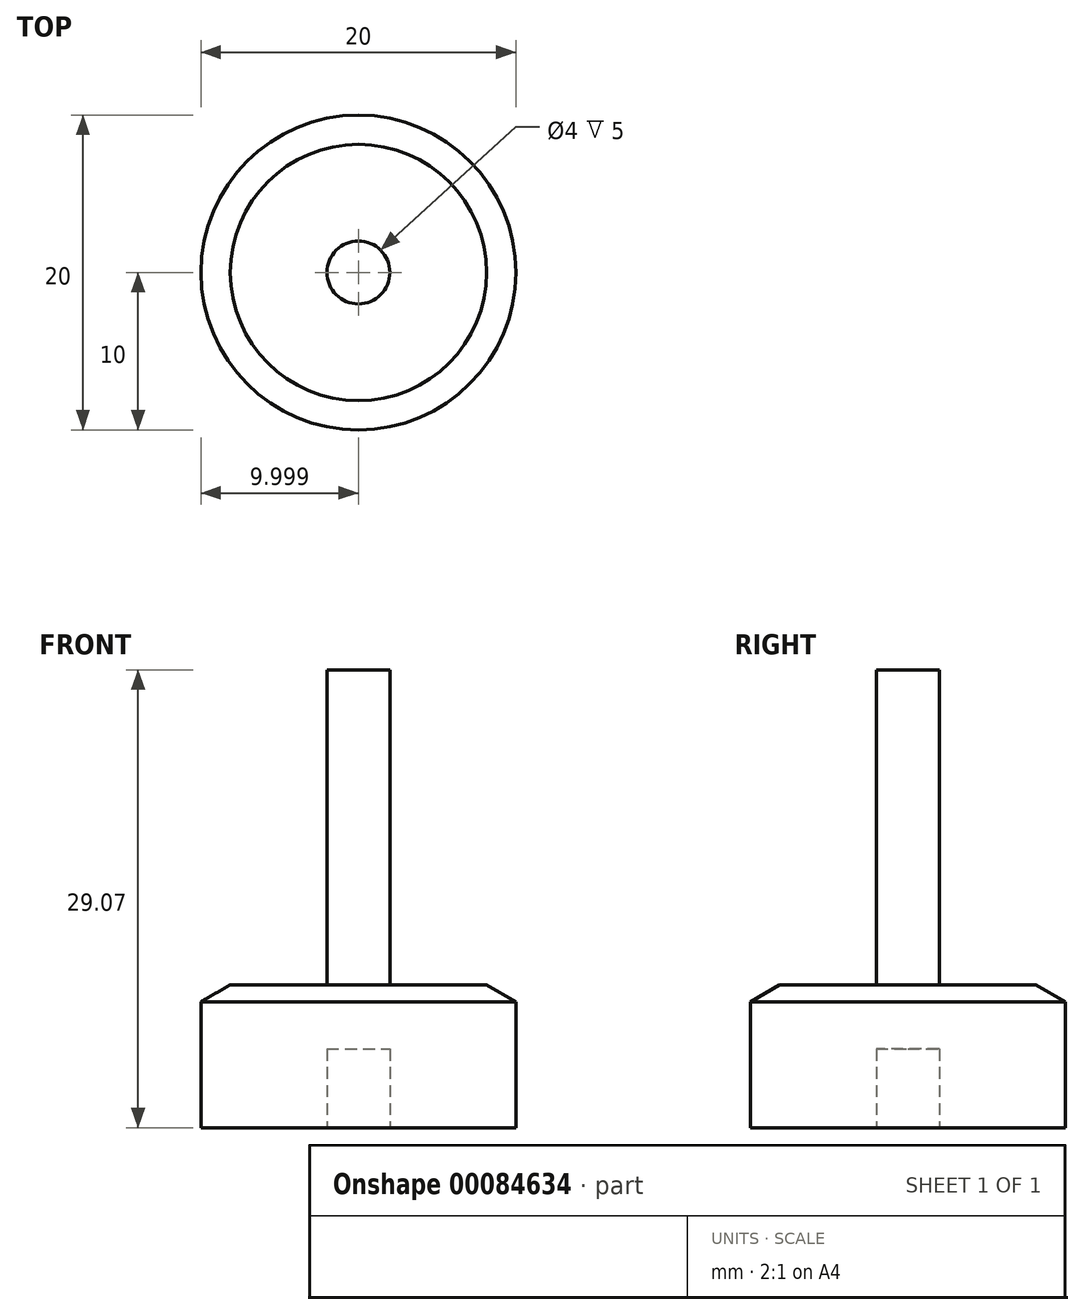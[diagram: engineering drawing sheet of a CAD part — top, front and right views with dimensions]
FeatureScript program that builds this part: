
annotation { "Feature Type Name" : "Feature", "Feature Type Description" : "" }
export const myFeature = defineFeature(function(context is Context, id is Id, definition is map)
    precondition{}
    {
        {
            var Q0;
            Q0=qCreatedBy(makeId("Front.planeOp"),FACE);
            var sketch = newSketch(context, id + "F0", { "sketchPlane" : qUnion([Q0])});
            skLineSegment(sketch, "E0.bottom", {"start": v(-30.55, 8) * mm, "end": v(-20.55, 8) * mm});
            skLineSegment(sketch, "E0.top", {"start": v(-30.55, 0) * mm, "end": v(-22.55, 0) * mm});
            skLineSegment(sketch, "E0.left", {"start": v(-30.55, 8) * mm, "end": v(-30.55, 0) * mm});
            skPoint(sketch, "E1", {"position": v(-20.55, 8) * mm});
            skPoint(sketch, "E2", {"position": v(-20.55, 0) * mm});
            skPoint(sketch, "E3", {"position": v(-20.55, 9.07) * mm});
            skLineSegment(sketch, "E4", {"start": v(-20.55, 8) * mm, "end": v(-20.55, 9.07) * mm});
            skLineSegment(sketch, "E5", {"start": v(-30.55, 8) * mm, "end": v(-28.7, 9.07) * mm});
            skLineSegment(sketch, "E6", {"start": v(-28.7, 9.07) * mm, "end": v(-20.55, 9.07) * mm});
            skLineSegment(sketch, "E7", {"start": v(-20.55, 8) * mm, "end": v(-20.55, 5) * mm});
            skPoint(sketch, "E0.right.end.orphan", {"position": v(-10.55, 0) * mm});
            skPoint(sketch, "E8.start.orphan", {"position": v(-10.55, 8) * mm});
            skLineSegment(sketch, "E9", {"start": v(-20.55, 9.07) * mm, "end": v(-20.55, 29.07) * mm});
            skLineSegment(sketch, "E10", {"start": v(-20.55, 29.07) * mm, "end": v(-22.55, 29.07) * mm});
            skLineSegment(sketch, "E11", {"start": v(-22.55, 29.07) * mm, "end": v(-22.55, 0) * mm});
            skPoint(sketch, "E12.start.orphan", {"position": v(-20.55, 4) * mm});
            skLineSegment(sketch, "E13", {"start": v(-20.55, 5) * mm, "end": v(-22.55, 5) * mm});
            skPoint(sketch, "E14", {"position": v(-20.55, 5) * mm});
            skSolve(sketch);
        }
        {
            var Q0;
            {var subQ0=sQuery(id+"F0.wireOp",EDGE,"E9");Q0=makeQuery(id+"F0.imprint","IMPRINT",FACE,{"disambiguationData":[TD([[makeQuery(id+"F0.imprint","IMPRINT",EDGE,{"derivedFrom":subQ0}),1.0]])]});}
            var Q1;
            {var subQ5=sQuery(id+"F0.wireOp",EDGE,"E0.top");Q1=makeQuery(id+"F0.imprint","IMPRINT",FACE,{"disambiguationData":[TD([[makeQuery(id+"F0.imprint","IMPRINT",EDGE,{"derivedFrom":subQ5}),1.0]])]});}
            var Q2;
            {var subQ0=sQuery(id+"F0.wireOp",EDGE,"E5");Q2=makeQuery(id+"F0.imprint","IMPRINT",FACE,{"disambiguationData":[TD([[makeQuery(id+"F0.imprint","IMPRINT",EDGE,{"derivedFrom":subQ0}),-1.0]])]});}
            var Q3;
            {var subQ0=sQuery(id+"F0.wireOp",EDGE,"E7");Q3=makeQuery(id+"F0.imprint","IMPRINT",FACE,{"disambiguationData":[TD([[makeQuery(id+"F0.imprint","IMPRINT",EDGE,{"derivedFrom":subQ0}),-1.0]])]});}
            var Q4;
            {var subQ0=sQuery(id+"F0.wireOp",EDGE,"E4");Q4=makeQuery(id+"F0.imprint","IMPRINT",FACE,{"disambiguationData":[TD([[makeQuery(id+"F0.imprint","IMPRINT",EDGE,{"derivedFrom":subQ0}),1.0]])]});}
            var Q5;
            Q5=sQuery(id+"F0.wireOp",EDGE,"E9");
            revolve(context, id + "F1", {"entities" : qUnion([Q0, Q1, Q2, Q3, Q4]), "axis" : qUnion([Q5]), "revolveType" : RevolveType.FULL});
        }
    });
